# Revit family: for update_36425XXX_NEW
name_source: partatom
category: Plumbing Fixtures
revit_build: Autodesk Revit 2018 (Build: 20170223_1515(x64)
units: mm (PartAtom-declared; Revit-internal decimal feet)

## family parameters
Always vertical = No
Cut with Voids When Loaded = No
OmniClass Number = 23.31.11.00
OmniClass Title = Faucets
Part Type = Normal
Room Calculation Point = No
Round Connector Dimension = Use Diameter
Shared = No
Work Plane-Based = Yes

## types (1)
- Default - please load Revit Family Type Catalog
    Always visible = Yes
    BIMobject category = Taps & Mixers
    Connector Description = Water Inlet 19.1mm
    Default Elevation = 1219 mm
    Description = AXOR Citterio E Bath Spout
    Design country = Germany
    Diameter = 19 mm
    EAN code = 4059625427668
    Edition number = 1
    GTIN code = https://4059625427668
    IFC Classification = Valve
    Manufacturer = AXOR
    Manufacturer country = Germany
    Manufacturer name = AXOR
    Material 1 = AXOR - Metal - 000 Chrome
    Model = 36425XXX
    OmniClass Code = 23-31 11 00
    OmniClass Description = Faucets
    Product Guid = 387a4739-e2a2-4d5d-8544-2fcdfb25c41c
    Product SKU = 36425XXX
    Product data url = https://bimobject.com
    Product family = AXOR Citterio E
    Product group = Bath fillers
    Product name = 36425XXX AXOR Citterio E Bath Spout
    QR code = https://bimobject.com
    URL = https://www.axor-design.com
    Weight Net (Kg) = 871

## geometry (parser evidence)
native form markers: Sweep x1
no freeform markers — native parametric forms only
